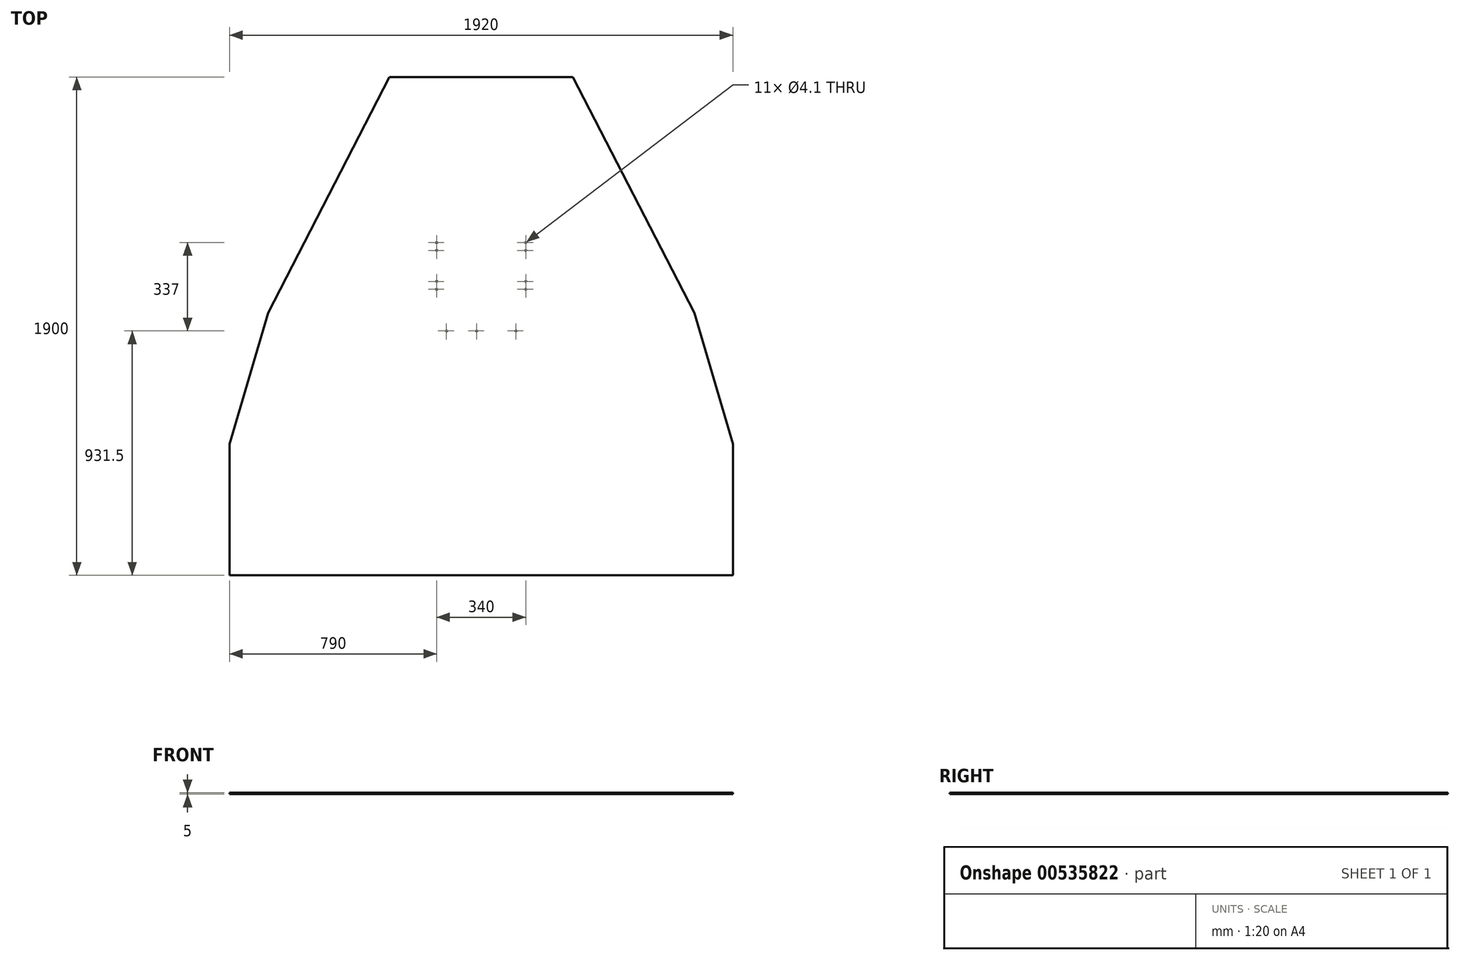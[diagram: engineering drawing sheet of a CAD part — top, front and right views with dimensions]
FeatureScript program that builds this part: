
annotation { "Feature Type Name" : "Feature", "Feature Type Description" : "" }
export const myFeature = defineFeature(function(context is Context, id is Id, definition is map)
    precondition{}
    {
        {
            var Q0;
            Q0=qCreatedBy(makeId("Top.planeOp"),FACE);
            var sketch = newSketch(context, id + "F0", { "sketchPlane" : qUnion([Q0])});
            skLineSegment(sketch, "E0.top", {"start": v(-960, -960) * mm, "end": v(960, -960) * mm});
            skLineSegment(sketch, "E0.left", {"start": v(-960, -460) * mm, "end": v(-960, -960) * mm});
            skLineSegment(sketch, "E0.right", {"start": v(960, -460) * mm, "end": v(960, -960) * mm});
            skLineSegment(sketch, "E1", {"start": v(0, 0) * mm, "end": v(0, -491.08) * mm, "construction": true});
            skCircle(sketch, "E2", {"center": v(170, 278.5) * mm, "radius": 2.05 * mm});
            skCircle(sketch, "E3", {"center": v(170, 308.5) * mm, "radius": 2.05 * mm});
            skCircle(sketch, "E4", {"center": v(170, 160.5) * mm, "radius": 2.05 * mm});
            skCircle(sketch, "E5", {"center": v(170, 130.5) * mm, "radius": 2.05 * mm});
            skCircle(sketch, "E6.MirrorC", {"center": v(-170, 130.5) * mm, "radius": 2.05 * mm});
            skCircle(sketch, "E7.MirrorC", {"center": v(-170, 160.5) * mm, "radius": 2.05 * mm});
            skCircle(sketch, "E8.MirrorC", {"center": v(-170, 278.5) * mm, "radius": 2.05 * mm});
            skCircle(sketch, "E9.MirrorC", {"center": v(-170, 308.5) * mm, "radius": 2.05 * mm});
            skCircle(sketch, "E10", {"center": v(-17.5, -28.5) * mm, "radius": 2.05 * mm});
            skCircle(sketch, "E11", {"center": v(-132.5, -28.5) * mm, "radius": 2.05 * mm});
            skCircle(sketch, "E12", {"center": v(132.5, -28.5) * mm, "radius": 2.05 * mm});
            skLineSegment(sketch, "E13", {"start": v(-192.5, 0) * mm, "end": v(192.5, 0) * mm, "construction": true});
            skLineSegment(sketch, "E14", {"start": v(-192.5, 0) * mm, "end": v(-192.5, -671.6) * mm, "construction": true});
            skLineSegment(sketch, "E15", {"start": v(-192.5, -671.6) * mm, "end": v(42.5, -671.6) * mm, "construction": true});
            skLineSegment(sketch, "E16", {"start": v(42.5, -671.6) * mm, "end": v(42.5, -164) * mm, "construction": true});
            skLineSegment(sketch, "E17", {"start": v(42.5, -164) * mm, "end": v(192.5, -164) * mm, "construction": true});
            skLineSegment(sketch, "E18", {"start": v(192.5, -164) * mm, "end": v(192.5, 0) * mm, "construction": true});
            skLineSegment(sketch, "E19.bottom", {"start": v(150, 110.5) * mm, "end": v(-150, 110.5) * mm, "construction": true});
            skLineSegment(sketch, "E19.top", {"start": v(150, 338.5) * mm, "end": v(-150, 338.5) * mm, "construction": true});
            skLineSegment(sketch, "E19.left", {"start": v(150, 110.5) * mm, "end": v(150, 338.5) * mm, "construction": true});
            skLineSegment(sketch, "E19.right", {"start": v(-150, 110.5) * mm, "end": v(-150, 338.5) * mm, "construction": true});
            skPoint(sketch, "E19.middle", {"position": v(0, 224.5) * mm});
            skLineSegment(sketch, "E20.bottom", {"start": v(-210, -760) * mm, "end": v(-710, -760) * mm, "construction": true});
            skLineSegment(sketch, "E20.top", {"start": v(-210, -160) * mm, "end": v(-710, -160) * mm, "construction": true});
            skLineSegment(sketch, "E20.left", {"start": v(-210, -760) * mm, "end": v(-210, -160) * mm, "construction": true});
            skLineSegment(sketch, "E20.right", {"start": v(-710, -760) * mm, "end": v(-710, -160) * mm, "construction": true});
            skPoint(sketch, "E20.middle", {"position": v(-460, -460) * mm});
            skLineSegment(sketch, "E21.bottom", {"start": v(-192.5, -676.6) * mm, "end": v(192.5, -676.6) * mm, "construction": true});
            skLineSegment(sketch, "E21.top", {"start": v(-192.5, -839.6) * mm, "end": v(192.5, -839.6) * mm, "construction": true});
            skLineSegment(sketch, "E21.left", {"start": v(-192.5, -676.6) * mm, "end": v(-192.5, -839.6) * mm, "construction": true});
            skLineSegment(sketch, "E21.right", {"start": v(192.5, -676.6) * mm, "end": v(192.5, -839.6) * mm, "construction": true});
            skLineSegment(sketch, "E22.MirrorCS", {"start": v(710, -760) * mm, "end": v(710, -160) * mm, "construction": true});
            skLineSegment(sketch, "E23.MirrorCS", {"start": v(210, -760) * mm, "end": v(710, -760) * mm, "construction": true});
            skLineSegment(sketch, "E24.MirrorCS", {"start": v(210, -160) * mm, "end": v(710, -160) * mm, "construction": true});
            skLineSegment(sketch, "E25.MirrorCS", {"start": v(210, -760) * mm, "end": v(210, -160) * mm, "construction": true});
            skLineSegment(sketch, "E26", {"start": v(-192.5, 40) * mm, "end": v(-812.5, 40) * mm, "construction": true});
            skLineSegment(sketch, "E27", {"start": v(-560, 90) * mm, "end": v(560, 90) * mm, "construction": true});
            skLineSegment(sketch, "E28", {"start": v(1326.36, -960) * mm, "end": v(1326.36, 940) * mm, "construction": true});
            skLineSegment(sketch, "E29", {"start": v(-350, 940) * mm, "end": v(350, 940) * mm});
            skLineSegment(sketch, "E30", {"start": v(192.5, 40) * mm, "end": v(812.5, 40) * mm, "construction": true});
            skLineSegment(sketch, "E31", {"start": v(-812.5, 40) * mm, "end": v(-960, -460) * mm});
            skLineSegment(sketch, "E32", {"start": v(960, -460) * mm, "end": v(812.5, 40) * mm});
            skLineSegment(sketch, "E33", {"start": v(-812.5, 40) * mm, "end": v(-350, 940) * mm});
            skLineSegment(sketch, "E34", {"start": v(350, 940) * mm, "end": v(812.5, 40) * mm});
            skLineSegment(sketch, "E35", {"start": v(-555.56, 540) * mm, "end": v(555.56, 540) * mm});
            skLineSegment(sketch, "E36", {"start": v(-320, -1097.3) * mm, "end": v(-320, -1020.96) * mm, "construction": true});
            skLineSegment(sketch, "E37", {"start": v(320, -1029.1) * mm, "end": v(320, -1086.82) * mm, "construction": true});
            skSolve(sketch);
        }
        {
            var Q0;
            Q0=qSketchRegion(id+"F0",true);
            extrude(context, id + "F1", {"entities" : qUnion([Q0]), "oppositeDirection" : true, "depth" : 5 * mm});
        }
    });
